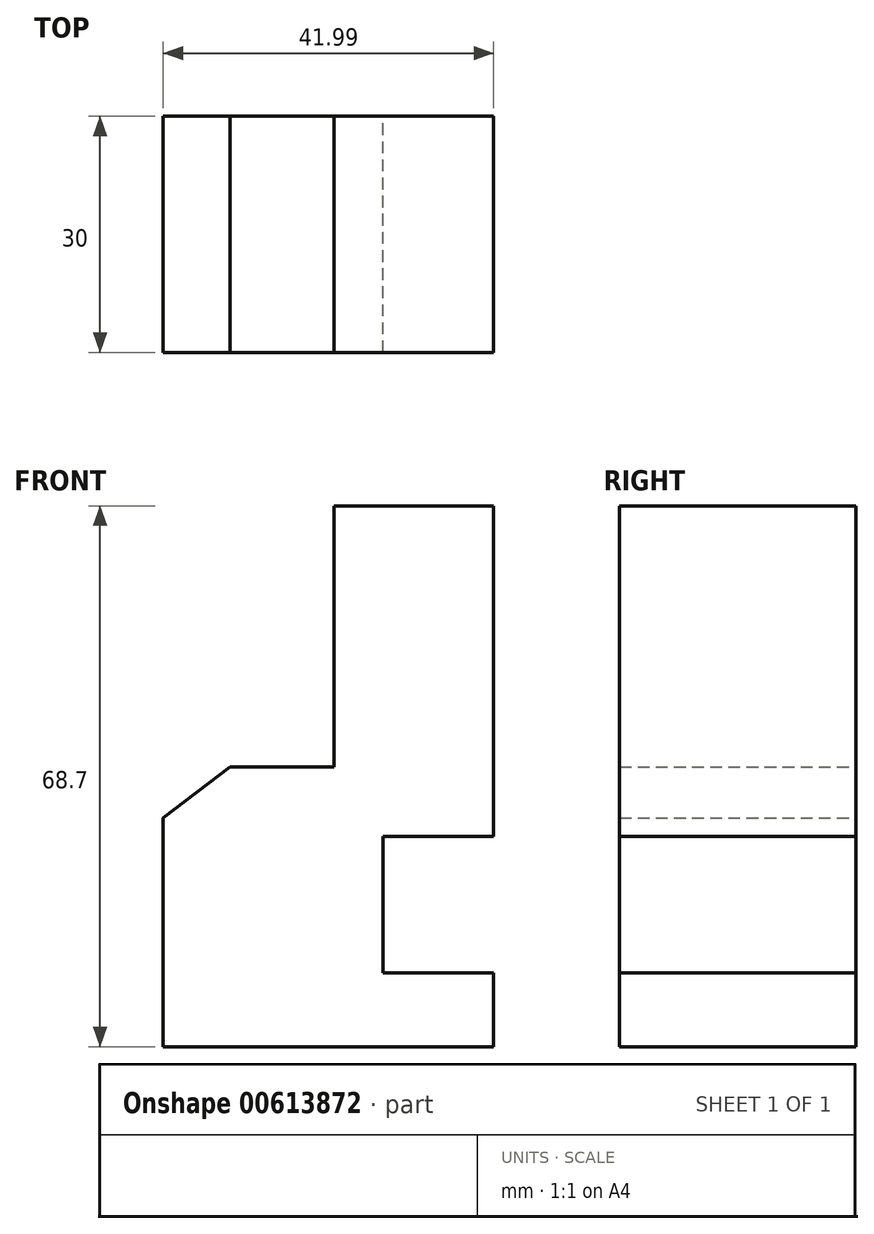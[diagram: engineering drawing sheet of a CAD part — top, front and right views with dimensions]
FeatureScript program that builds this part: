
annotation { "Feature Type Name" : "Feature", "Feature Type Description" : "" }
export const myFeature = defineFeature(function(context is Context, id is Id, definition is map)
    precondition{}
    {
        {
            var Q0;
            Q0=qCreatedBy(makeId("Front.planeOp"),FACE);
            var sketch = newSketch(context, id + "F0", { "sketchPlane" : qUnion([Q0])});
            skLineSegment(sketch, "E0.bottom", {"start": v(9.54, 26.13) * mm, "end": v(29.8, 26.13) * mm});
            skLineSegment(sketch, "E0.top", {"start": v(15.7, -15.86) * mm, "end": v(29.8, -15.86) * mm});
            skLineSegment(sketch, "E0.left", {"start": v(9.54, 26.13) * mm, "end": v(9.54, -7.05) * mm});
            skLineSegment(sketch, "E0.right", {"start": v(29.8, 26.13) * mm, "end": v(29.8, -15.86) * mm});
            skLineSegment(sketch, "E1", {"start": v(9.54, -7.05) * mm, "end": v(-3.67, -7.05) * mm});
            skLineSegment(sketch, "E2", {"start": v(-3.67, -7.05) * mm, "end": v(-12.19, -13.5) * mm});
            skLineSegment(sketch, "E3", {"start": v(-12.19, -13.5) * mm, "end": v(-12.19, -42.57) * mm});
            skPoint(sketch, "E4.end.orphan", {"position": v(9.54, -42.57) * mm});
            skLineSegment(sketch, "E5", {"start": v(-12.19, -42.57) * mm, "end": v(15.7, -42.57) * mm});
            skLineSegment(sketch, "E6", {"start": v(15.7, -33.18) * mm, "end": v(15.7, -15.86) * mm});
            skLineSegment(sketch, "E7.bottom", {"start": v(15.7, -42.57) * mm, "end": v(29.8, -42.57) * mm});
            skLineSegment(sketch, "E7.top", {"start": v(15.7, -33.18) * mm, "end": v(29.8, -33.18) * mm});
            skLineSegment(sketch, "E7.right", {"start": v(29.8, -42.57) * mm, "end": v(29.8, -33.18) * mm});
            skPoint(sketch, "E8.orphan", {"position": v(9.54, -15.86) * mm});
            skSolve(sketch);
        }
        {
            var Q0;
            Q0 = qSketchRegion(id + "F0", true);
            extrude(context, id + "F1", {"entities" : qUnion([Q0]), "depth" : 30 * mm, "offsetDistance" : 25 * mm});
        }
    });
